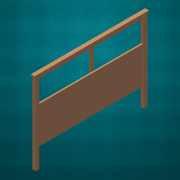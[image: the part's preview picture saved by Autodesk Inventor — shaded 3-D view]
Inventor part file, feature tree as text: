
AUTODESK INVENTOR PART (.ipt)
format: ipt  version: 2017 (Build 210142000, 142)  size: 264,704 bytes
history: native  units: in
note: dims shown in document units (in); Inventor stores cm internally (conversion verified against a paired STEP export)
features: extrude x5, sketch x4, chamfer x1, pattern_linear x1
ambient origin geometry x8: Origin, YZ Plane, XZ Plane, XY Plane, X Axis, Y Axis, Z Axis, Center Point
bodies: Solid1 (feature_tree), Solid2 (feature_tree)
feature tree (11):
  extrude  "Extrusion1"  Depth=2.25in
  extrude  "Extrusion2"  Depth=46.25in TaperAngle=0.0deg
  extrude  "Extrusion3"  Depth=0.875in
  extrude  "Extrusion4"  Depth=2.25in
  chamfer  "Chamfer1"  Distance=0.875in
  pattern_linear  "Rectangular Pattern1"  Spacing1=65.75in  [1 undecoded]
  extrude  "Extrusion5"  Depth=0.5in
  sketch  "Sketch1"  dims[d0=1.875in d1=2.25in]
  sketch  "Sketch2"  dims[d2=63.875in d3=46.25in d4=0.0in]
  sketch  "Sketch3"  dims[d5=2.125in d6=0.875in]
  sketch  "Sketch5"  dims[d7=65.0in d8=0.0in d9=2.25in d10=0.875in d12=65.75in d13=0.0in d15=0.5in d16=2.25in d17=65.75in d18=0.0in d19=0.0625in d20=0.125in d21=45.0deg d22=0.25in d23=8.0in d24=1.5748in d26=5.0in d27=0.25in d28=19.0in d29=0.0in d30=12.375in d31=1.9685in d33=5.0in d34=2.5in]
note: 1 required parameter value undecoded (feature->parameter linkage not recoverable at this tier; creation-order binding heuristic only, values carry confidence <= 0.55)
